# Revit family: Specialty_Equipment-Bavis_Fabacraft-Basic_Drive-Up_Window NEW
name_source: partatom
category: Specialty Equipment
units: mm (PartAtom-declared; Revit-internal decimal feet)

## family parameters
Always vertical = Yes
Cut with Voids When Loaded = No
Host = Wall
OmniClass Number = 23.40.70.27.24.21
OmniClass Title = Service and Teller Window Units
Part Type = Normal
Room Calculation Point = No
Round Connector Dimension = Use Diameter
Shared = No

## types (4) — shared parameters
Assembly Code = B2020100
Default Elevation = 0' - 0"
Depth = 0' - 5 1/2"
Finish = Metal - Bavis Fabacraft -Aluminum
Glazing = Glass - Bavis Fabacraft - Clear
Instruction Sheet Link = https://docs.bavis.com
Keynote = 08 51 00
Manufacturer = Bavis Fabacraft
Product Documentation Link = https://docs.bavis.com
Product Name = Bavis Basic Drive-Up Windows
Product Page URL = https://www.bavis.com
URL = https://www.bavis.com
Version = 2020 - v1.0a
Video Link = https://www.youtube.com

## per-type parameters (varying)
| type | Constraints | Height | Model | Rough Height | Rough Width | Warranty URL | Width |
| 60" Trimless | 60 | 2' - 9 1/4" | 12147992 | 2' - 9 1/2" | 4' - 8 1/2" |  | 4' - 8" |
| 32" Trimless | 32 | 2' - 9 1/4" | 12147991 | 2' - 9 1/2" | 2' - 8 1/2" | Contact Manufacturer for Warranty Information | 2' - 8" |
| 42" Trimless | 42 | 2' - 11 7/8" | 12147996 | 3' - 0 1/8" | 3' - 6 3/4" |  | 3' - 6 1/4" |
| 65" Trimless | 65 | 2' - 11 7/8" | 12147995 | 3' - 0 1/8" | 5' - 5 3/8" |  | 5' - 4 7/8" |

## geometry (parser evidence)
native form markers: Sweep x3
no freeform markers — native parametric forms only
